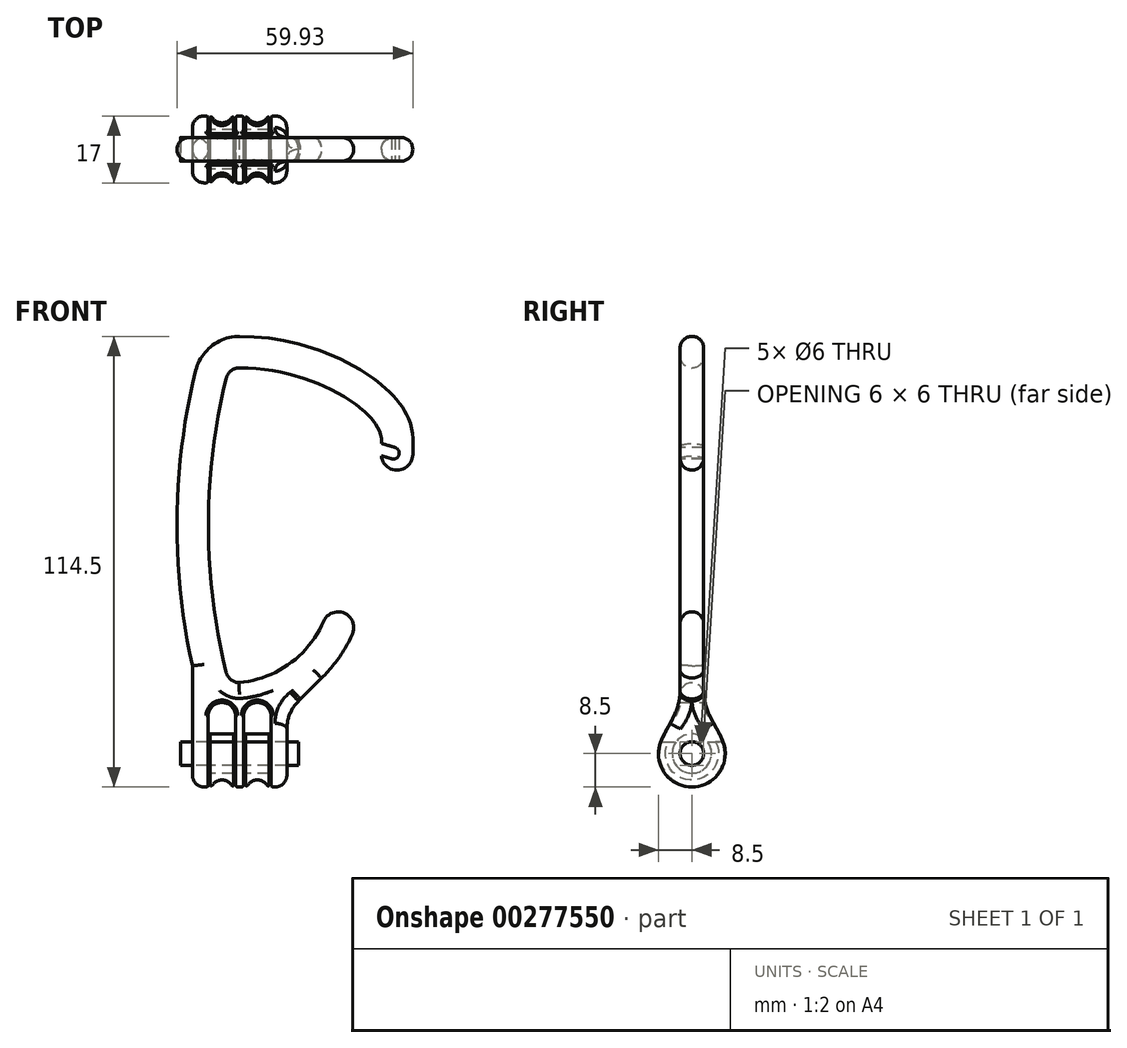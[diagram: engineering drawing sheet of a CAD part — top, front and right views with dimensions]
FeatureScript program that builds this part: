
annotation { "Feature Type Name" : "Feature", "Feature Type Description" : "" }
export const myFeature = defineFeature(function(context is Context, id is Id, definition is map)
    precondition{}
    {
        {
            var Q0;
            Q0=qCreatedBy(makeId("Front.planeOp"),FACE);
            var sketch = newSketch(context, id + "F0", { "sketchPlane" : qUnion([Q0])});
            skPoint(sketch, "E0.middle", {"position": v(0, 0) * mm});
            skLineSegment(sketch, "E1", {"start": v(0, 91.6) * mm, "end": v(0, -27.1) * mm, "construction": true});
            skLineSegment(sketch, "E2", {"start": v(-37.43, 0) * mm, "end": v(37.27, 0) * mm, "construction": true});
            skLineSegment(sketch, "E3", {"start": v(-37.5, -22) * mm, "end": v(37.5, -22) * mm, "construction": true});
            skLineSegment(sketch, "E4", {"start": v(-4.5, -27) * mm, "end": v(-4.5, -17) * mm, "construction": true});
            skLineSegment(sketch, "E5", {"start": v(4.5, -27) * mm, "end": v(4.5, -17) * mm, "construction": true});
            skLineSegment(sketch, "E6", {"start": v(-5, 80) * mm, "end": v(5, 80) * mm, "construction": true});
            skSolve(sketch);
        }
        {
            var Q0;
            Q0=qCreatedBy(makeId("Front.planeOp"),FACE);
            var sketch = newSketch(context, id + "F1", { "sketchPlane" : qUnion([Q0])});
            skLineSegment(sketch, "E7", {"start": v(-7.5, -17) * mm, "end": v(-7.5, -14) * mm});
            skLineSegment(sketch, "E8", {"start": v(-1.5, -14) * mm, "end": v(-1.5, -17) * mm});
            skArc(sketch, "E9", {"start": v(-7.04, -13.87) * mm, "mid": v(-4.5, -15.27) * mm, "end": v(-1.96, -13.87) * mm});
            skPoint(sketch, "E10.visualSharp", {"position": v(-7.5, -12.27) * mm});
            skArc(sketch, "E10.filletArc", {"start": v(-7.04, -13.87) * mm, "mid": v(-7.32, -13.76) * mm, "end": v(-7.5, -14) * mm});
            skPoint(sketch, "E11.visualSharp", {"position": v(-1.5, -12.27) * mm});
            skArc(sketch, "E11.filletArc", {"start": v(-1.5, -14) * mm, "mid": v(-1.68, -13.76) * mm, "end": v(-1.96, -13.87) * mm});
            skLineSegment(sketch, "E12", {"start": v(-7.5, -17) * mm, "end": v(-1.5, -17) * mm});
            skArc(sketch, "E13.MirrorCS", {"start": v(7.04, -13.87) * mm, "mid": v(7.32, -13.76) * mm, "end": v(7.5, -14) * mm});
            skArc(sketch, "E14.MirrorCS", {"start": v(1.5, -14) * mm, "mid": v(1.68, -13.76) * mm, "end": v(1.96, -13.87) * mm});
            skArc(sketch, "E15.MirrorCS", {"start": v(7.04, -13.87) * mm, "mid": v(4.5, -15.27) * mm, "end": v(1.96, -13.87) * mm});
            skPoint(sketch, "E16.MirrorP", {"position": v(7.5, -12.27) * mm});
            skPoint(sketch, "E17.MirrorP", {"position": v(1.5, -12.27) * mm});
            skLineSegment(sketch, "E18.MirrorCS", {"start": v(1.5, -14) * mm, "end": v(1.5, -17) * mm});
            skLineSegment(sketch, "E19.MirrorCS", {"start": v(7.5, -17) * mm, "end": v(1.5, -17) * mm});
            skLineSegment(sketch, "E20.MirrorCS", {"start": v(7.5, -17) * mm, "end": v(7.5, -14) * mm});
            skSolve(sketch);
        }
        {
            var Q0;
            Q0 = qSketchRegion(id + "F1", true);
            var Q1;
            Q1=sQuery(id+"F0.wireOp",EDGE,"E3");
            revolve(context, id + "F2", {"entities" : qUnion([Q0]), "axis" : qUnion([Q1]), "revolveType" : RevolveType.FULL});
        }
        {
            var Q0;
            Q0=qCreatedBy(makeId("Front.planeOp"),FACE);
            var sketch = newSketch(context, id + "F3", { "sketchPlane" : qUnion([Q0])});
            skPoint(sketch, "E21", {"position": v(0, 80) * mm});
            skPoint(sketch, "E22", {"position": v(40, 58) * mm});
            skArc(sketch, "E23", {"start": v(0, 80) * mm, "mid": v(-4.63, 78.4) * mm, "end": v(-7.28, 74.3) * mm});
            skPoint(sketch, "E24", {"position": v(25, 10) * mm});
            skLineSegment(sketch, "E25", {"start": v(40, 58) * mm, "end": v(40, 54) * mm});
            skArc(sketch, "E26", {"start": v(-7.28, -2.3) * mm, "mid": v(-4.63, -6.4) * mm, "end": v(0, -8) * mm});
            skArc(sketch, "E27", {"start": v(0, -8) * mm, "mid": v(14.99, -2.45) * mm, "end": v(25, 10) * mm});
            skFitSpline(sketch, "E28", {"points": [v(0, 80) * mm, v(40, 58) * mm], "startDerivative": vector(60, 0) * mm, "endDerivative": vector(0, -30) * mm});
            skPoint(sketch, "E29", {"position": v(40, 54) * mm});
            skArc(sketch, "E30", {"start": v(-7.28, 74.3) * mm, "mid": v(-11.93, 36) * mm, "end": v(-7.28, -2.3) * mm});
            skSolve(sketch);
        }
        {
            var Q0;
            Q0=qCreatedBy(makeId("Top.planeOp"),FACE);
            cPlane(context, id + "F4", {"entities" : qUnion([Q0]), "cplaneType" : CPlaneType.OFFSET, "offset" : 54 * mm, "width" : 150 * mm, "height" : 150 * mm});
        }
        {
            var Q0;
            Q0=qCreatedBy(id+"F4.planeOp",FACE);
            var sketch = newSketch(context, id + "F5", { "sketchPlane" : qUnion([Q0])});
            skLineSegment(sketch, "E31.bottom", {"start": v(39, -3) * mm, "end": v(41, -3) * mm});
            skLineSegment(sketch, "E31.top", {"start": v(39, 3) * mm, "end": v(41, 3) * mm});
            skArc(sketch, "E32", {"start": v(39, 3) * mm, "mid": v(36, 0) * mm, "end": v(39, -3) * mm});
            skArc(sketch, "E33", {"start": v(41, -3) * mm, "mid": v(44, 0) * mm, "end": v(41, 3) * mm});
            skSolve(sketch);
        }
        {
            var Q0;
            Q0=makeQuery(id+"F5.imprint","IMPRINT",FACE,{"disambiguationData":[TD([[makeQuery(id+"F5.imprint","IMPRINT",EDGE,{"derivedFrom":sQuery(id+"F5.wireOp",EDGE,"E31.bottom")}),1.0]])]});
            var Q1;
            Q1=sQuery(id+"F3.wireOp",EDGE,"E25");
            var Q2;
            Q2=sQuery(id+"F3.wireOp",EDGE,"E28");
            var Q3;
            Q3=sQuery(id+"F3.wireOp",EDGE,"E23");
            var Q4;
            Q4=sQuery(id+"F3.wireOp",EDGE,"57eace3e-279f-4ff9-bc42-776380e31d05");
            var Q5;
            Q5=sQuery(id+"F3.wireOp",EDGE,"E26");
            var Q6;
            Q6=sQuery(id+"F3.wireOp",EDGE,"E27");
            var Q7;
            Q7=sQuery(id+"F3.wireOp",EDGE,"E30");
            sweep(context, id + "F6", {"profiles" : qUnion([Q0]), "path" : qUnion([Q1, Q2, Q3, Q4, Q5, Q6, Q7])});
        }
        {
            var Q0;
            Q0=qCreatedBy(makeId("Front.planeOp"),FACE);
            var sketch = newSketch(context, id + "F7", { "sketchPlane" : qUnion([Q0])});
            skLineSegment(sketch, "E34", {"start": v(-8, -17.5) * mm, "end": v(-8, -30.5) * mm});
            skLineSegment(sketch, "E35", {"start": v(-8, -30.5) * mm, "end": v(-12, -30.5) * mm});
            skLineSegment(sketch, "E36", {"start": v(-12, -30.5) * mm, "end": v(-12, -14.5) * mm});
            skLineSegment(sketch, "E37", {"start": v(0, -30.5) * mm, "end": v(-1, -30.5) * mm});
            skLineSegment(sketch, "E38", {"start": v(-1, -30.5) * mm, "end": v(-1, -17.5) * mm});
            skArc(sketch, "E39", {"start": v(-1, -17.5) * mm, "mid": v(-4.5, -14) * mm, "end": v(-8, -17.5) * mm});
            skLineSegment(sketch, "E40.MirrorCS", {"start": v(0, -30.5) * mm, "end": v(1, -30.5) * mm});
            skArc(sketch, "E41.MirrorCS", {"start": v(1, -17.5) * mm, "mid": v(4.5, -14) * mm, "end": v(8, -17.5) * mm});
            skLineSegment(sketch, "E42.MirrorCS", {"start": v(8, -17.5) * mm, "end": v(8, -30.5) * mm});
            skLineSegment(sketch, "E43.MirrorCS", {"start": v(1, -30.5) * mm, "end": v(1, -17.5) * mm});
            skLineSegment(sketch, "E44.MirrorCS", {"start": v(12, -30.5) * mm, "end": v(12, -15.77) * mm});
            skLineSegment(sketch, "E45.MirrorCS", {"start": v(8, -30.5) * mm, "end": v(12, -30.5) * mm});
            skArc(sketch, "E46", {"start": v(-7.17, -2.73) * mm, "mid": v(-4.46, -6.56) * mm, "end": v(0, -8.03) * mm});
            skArc(sketch, "E47", {"start": v(0, -8.03) * mm, "mid": v(9.66, -5.53) * mm, "end": v(17.97, 0) * mm});
            skLineSegment(sketch, "E48", {"start": v(17.97, 0) * mm, "end": v(20.8, -2.83) * mm});
            skLineSegment(sketch, "E49", {"start": v(-12, -14.5) * mm, "end": v(-12, 25.5) * mm});
            skLineSegment(sketch, "E50", {"start": v(-12, 25.5) * mm, "end": v(-7.17, -2.73) * mm});
            skLineSegment(sketch, "E51", {"start": v(20.8, -2.83) * mm, "end": v(14.93, -8.7) * mm});
            skPoint(sketch, "E52.visualSharp", {"position": v(12, -11.63) * mm});
            skArc(sketch, "E52.filletArc", {"start": v(14.93, -8.7) * mm, "mid": v(12.76, -11.94) * mm, "end": v(12, -15.77) * mm});
            skSolve(sketch);
        }
        {
            var Q0;
            Q0=makeQuery(id+"F7.imprint","IMPRINT",FACE,{"disambiguationData":[TD([[makeQuery(id+"F7.imprint","IMPRINT",EDGE,{"derivedFrom":sQuery(id+"F7.wireOp",EDGE,"E34")}),-1.0]])]});
            extrude(context, id + "F8", {"entities" : qUnion([Q0]), "operationType" : NewBodyOperationType.ADD, "endBound" : BoundingType.SYMMETRIC, "depth" : 18 * mm});
        }
        {
            var Q0;
            Q0=qCreatedBy(makeId("Right.planeOp"),FACE);
            var sketch = newSketch(context, id + "F9", { "sketchPlane" : qUnion([Q0])});
            skArc(sketch, "E53", {"start": v(-8.5, -22) * mm, "mid": v(0, -30.5) * mm, "end": v(8.5, -22) * mm});
            skFitSpline(sketch, "E54", {"points": [v(8.5, -22) * mm, v(3, -6) * mm], "startDerivative": vector(0, 15) * mm, "endDerivative": vector(0, 21) * mm});
            skFitSpline(sketch, "E55.MirrorCS", {"points": [v(-8.5, -22) * mm, v(-3, -6) * mm], "startDerivative": vector(0, 15) * mm, "endDerivative": vector(0, 21) * mm});
            skLineSegment(sketch, "E56", {"start": v(-3, -6) * mm, "end": v(-3, 30) * mm});
            skLineSegment(sketch, "E57", {"start": v(-3, 30) * mm, "end": v(-13, 30) * mm});
            skLineSegment(sketch, "E58", {"start": v(-13, -40) * mm, "end": v(-13, 30) * mm});
            skLineSegment(sketch, "E59.MirrorCS", {"start": v(13, -40) * mm, "end": v(13, 30) * mm});
            skLineSegment(sketch, "E60.MirrorCS", {"start": v(3, 30) * mm, "end": v(13, 30) * mm});
            skLineSegment(sketch, "E61", {"start": v(3, 30) * mm, "end": v(3, -6) * mm});
            skCircle(sketch, "E62", {"center": v(0, -22) * mm, "radius": 3 * mm});
            skLineSegment(sketch, "E63", {"start": v(13, -40) * mm, "end": v(-13, -40) * mm});
            skSolve(sketch);
        }
        {
            var Q0;
            Q0=makeQuery(id+"F9.imprint","IMPRINT",FACE,{"disambiguationData":[TD([[makeQuery(id+"F9.imprint","IMPRINT",EDGE,{"derivedFrom":sQuery(id+"F9.wireOp",EDGE,"E53")}),-1.0]])]});
            extrude(context, id + "F10", {"entities" : qUnion([Q0]), "operationType" : NewBodyOperationType.REMOVE, "endBound" : BoundingType.SYMMETRIC, "depth" : 100 * mm});
        }
        {
            var Q0;
            Q0=makeQuery(id+"F6.opSweep","CAP_FACE",FACE,{"disambiguationData":[OSD([sQuery(id+"F3.wireOp",VERTEX,"E27.end"),sQuery(id+"F5.wireOp",EDGE,"E31.bottom"),sQuery(id+"F5.wireOp",EDGE,"E31.top"),sQuery(id+"F5.wireOp",EDGE,"E32"),sQuery(id+"F5.wireOp",EDGE,"E33")])],"isStart":false});
            var sketch = newSketch(context, id + "F11", { "sketchPlane" : qUnion([Q0])});
            skLineSegment(sketch, "E64", {"start": v(18.99, -3) * mm, "end": v(18.99, 3) * mm});
            skLineSegment(sketch, "E65", {"start": v(18.99, 3) * mm, "end": v(19.99, 3) * mm});
            skLineSegment(sketch, "E66", {"start": v(18.99, -3) * mm, "end": v(19.99, -3) * mm});
            skArc(sketch, "E67", {"start": v(19.99, -3) * mm, "mid": v(22.99, 0) * mm, "end": v(19.99, 3) * mm});
            skLineSegment(sketch, "E68", {"start": v(18.99, 4.4) * mm, "end": v(18.99, -4.85) * mm, "construction": true});
            skSolve(sketch);
        }
        {
            var Q0;
            Q0 = qSketchRegion(id + "F11", true);
            var Q1;
            Q1=sQuery(id+"F11.wireOp",EDGE,"E68");
            revolve(context, id + "F12", {"operationType" : NewBodyOperationType.ADD, "entities" : qUnion([Q0]), "axis" : qUnion([Q1]), "revolveType" : RevolveType.FULL});
        }
        {
            var Q0;
            Q0=makeQuery(id+"F6.opSweep","CAP_FACE",FACE,{"disambiguationData":[OSD([sQuery(id+"F3.wireOp",VERTEX,"E25.end"),sQuery(id+"F5.wireOp",EDGE,"E31.bottom"),sQuery(id+"F5.wireOp",EDGE,"E31.top"),sQuery(id+"F5.wireOp",EDGE,"E32"),sQuery(id+"F5.wireOp",EDGE,"E33")])],"isStart":true});
            var sketch = newSketch(context, id + "F13", { "sketchPlane" : qUnion([Q0])});
            skLineSegment(sketch, "E69", {"start": v(40, -3) * mm, "end": v(40, 3) * mm});
            skLineSegment(sketch, "E70", {"start": v(40, -3) * mm, "end": v(41, -3) * mm});
            skLineSegment(sketch, "E71", {"start": v(40, 4.32) * mm, "end": v(40, -4) * mm, "construction": true});
            skLineSegment(sketch, "E72", {"start": v(40, 3) * mm, "end": v(41, 3) * mm});
            skArc(sketch, "E73", {"start": v(41, -3) * mm, "mid": v(44, 0) * mm, "end": v(41, 3) * mm});
            skSolve(sketch);
        }
        {
            var Q0;
            Q0 = qSketchRegion(id + "F13", true);
            var Q1;
            Q1=sQuery(id+"F13.wireOp",EDGE,"E71");
            revolve(context, id + "F14", {"operationType" : NewBodyOperationType.ADD, "entities" : qUnion([Q0]), "axis" : qUnion([Q1]), "revolveType" : RevolveType.FULL});
        }
        {
            var Q0;
            Q0=qCreatedBy(makeId("Front.planeOp"),FACE);
            var sketch = newSketch(context, id + "F15", { "sketchPlane" : qUnion([Q0])});
            skPoint(sketch, "E74", {"position": v(23.17, 6.44) * mm});
            skPoint(sketch, "E75", {"position": v(20.89, 3.16) * mm});
            skCircle(sketch, "E76", {"center": v(23.17, 6.44) * mm, "radius": 50.45 * mm, "construction": true});
            skArc(sketch, "E77", {"start": v(37.63, 54.8) * mm, "mid": v(37.63, 54.79) * mm, "end": v(37.62, 54.78) * mm});
            skLineSegment(sketch, "E78", {"start": v(39.05, 54.32) * mm, "end": v(39.53, 55.75) * mm});
            skLineSegment(sketch, "E79", {"start": v(39.05, 54.32) * mm, "end": v(38.58, 52.9) * mm});
            skLineSegment(sketch, "E80", {"start": v(39.05, 54.32) * mm, "end": v(33.18, 56.27) * mm, "construction": true});
            skArc(sketch, "E81.trimOffspring", {"start": v(38.58, 52.9) * mm, "mid": v(40.48, 53.85) * mm, "end": v(39.53, 55.75) * mm});
            skArc(sketch, "E82", {"start": v(39.53, 55.75) * mm, "mid": v(37.61, 56.32) * mm, "end": v(35.68, 56.86) * mm});
            skArc(sketch, "E83", {"start": v(38.58, 52.9) * mm, "mid": v(36.66, 53.47) * mm, "end": v(34.74, 54) * mm});
            skLineSegment(sketch, "E84", {"start": v(35.68, 56.86) * mm, "end": v(34.74, 54) * mm});
            skSolve(sketch);
        }
        {
            var Q0;
            Q0 = qSketchRegion(id + "F15", true);
            extrude(context, id + "F16", {"entities" : qUnion([Q0]), "operationType" : NewBodyOperationType.REMOVE, "endBound" : BoundingType.SYMMETRIC, "oppositeDirection" : true, "depth" : 25 * mm});
        }
        {
            var Q0;
            Q0=makeQuery(id+"F10.boolean.opBoolean","INTERSECT",EDGE,{"derivedFrom":[makeQuery(id+"F8.opExtrude","SWEPT_FACE",FACE,{"disambiguationData":[OSD([sQuery(id+"F7.wireOp",EDGE,"E36"),sQuery(id+"F7.wireOp",EDGE,"E49")])]}),makeQuery(id+"F10.opExtrude","SWEPT_FACE",FACE,{"disambiguationData":[OSD([sQuery(id+"F9.wireOp",EDGE,"E56")])]})]});
            var Q1;
            Q1=makeQuery(id+"F10.boolean.opBoolean","INTERSECT",EDGE,{"derivedFrom":[makeQuery(id+"F8.opExtrude","SWEPT_FACE",FACE,{"disambiguationData":[OSD([sQuery(id+"F7.wireOp",EDGE,"E36"),sQuery(id+"F7.wireOp",EDGE,"E49")])]}),makeQuery(id+"F10.opExtrude","SWEPT_FACE",FACE,{"disambiguationData":[OSD([sQuery(id+"F9.wireOp",EDGE,"E61")])]})]});
            var Q2;
            Q2=makeQuery(id+"F10.boolean.opBoolean","INTERSECT",EDGE,{"derivedFrom":[makeQuery(id+"F8.opExtrude","SWEPT_FACE",FACE,{"disambiguationData":[OSD([sQuery(id+"F7.wireOp",EDGE,"E36"),sQuery(id+"F7.wireOp",EDGE,"E49")])]}),makeQuery(id+"F10.opExtrude","SWEPT_FACE",FACE,{"disambiguationData":[OSD([sQuery(id+"F9.wireOp",EDGE,"E55.MirrorCS")])]})]});
            var Q3;
            Q3=makeQuery(id+"F10.boolean.opBoolean","INTERSECT",EDGE,{"derivedFrom":[makeQuery(id+"F8.opExtrude","SWEPT_FACE",FACE,{"disambiguationData":[OSD([sQuery(id+"F7.wireOp",EDGE,"E36"),sQuery(id+"F7.wireOp",EDGE,"E49")])]}),makeQuery(id+"F10.opExtrude","SWEPT_FACE",FACE,{"disambiguationData":[OSD([sQuery(id+"F9.wireOp",EDGE,"E53")])]})]});
            var Q4;
            Q4=makeQuery(id+"F10.boolean.opBoolean","INTERSECT",EDGE,{"derivedFrom":[makeQuery(id+"F8.opExtrude","SWEPT_FACE",FACE,{"disambiguationData":[OSD([sQuery(id+"F7.wireOp",EDGE,"E36"),sQuery(id+"F7.wireOp",EDGE,"E49")])]}),makeQuery(id+"F10.opExtrude","SWEPT_FACE",FACE,{"disambiguationData":[OSD([sQuery(id+"F9.wireOp",EDGE,"E54")])]})]});
            fillet(context, id + "F17", {"entities" : qUnion([Q0, Q1, Q2, Q3, Q4]), "radius" : 3 * mm, "tangentPropagation" : true, "allowEdgeOverflow" : false});
        }
        {
            var Q0;
            Q0=qCreatedBy(makeId("Front.planeOp"),FACE);
            var sketch = newSketch(context, id + "F18", { "sketchPlane" : qUnion([Q0])});
            skArc(sketch, "E85", {"start": v(8, -12.5) * mm, "mid": v(4.5, -9) * mm, "end": v(1, -12.5) * mm});
            skLineSegment(sketch, "E86.top", {"start": v(8, -19) * mm, "end": v(1, -19) * mm});
            skLineSegment(sketch, "E86.left", {"start": v(8, -12.5) * mm, "end": v(8, -19) * mm});
            skLineSegment(sketch, "E86.right", {"start": v(1, -12.5) * mm, "end": v(1, -19) * mm});
            skLineSegment(sketch, "E87.MirrorCS", {"start": v(-8, -12.5) * mm, "end": v(-8, -19) * mm});
            skLineSegment(sketch, "E88.MirrorCS", {"start": v(-1, -12.5) * mm, "end": v(-1, -19) * mm});
            skLineSegment(sketch, "E89.MirrorCS", {"start": v(-8, -19) * mm, "end": v(-1, -19) * mm});
            skArc(sketch, "E90.MirrorCS", {"start": v(-8, -12.5) * mm, "mid": v(-4.5, -9) * mm, "end": v(-1, -12.5) * mm});
            skSolve(sketch);
        }
        {
            var Q0;
            Q0 = qSketchRegion(id + "F18", true);
            extrude(context, id + "F19", {"entities" : qUnion([Q0]), "operationType" : NewBodyOperationType.REMOVE, "endBound" : BoundingType.SYMMETRIC, "depth" : 25 * mm});
        }
        {
            var Q0;
            Q0=makeQuery(id+"F10.boolean.opBoolean","INTERSECT",EDGE,{"derivedFrom":[makeQuery(id+"F8.opExtrude","SWEPT_FACE",FACE,{"disambiguationData":[OSD([sQuery(id+"F7.wireOp",EDGE,"E51")])]}),makeQuery(id+"F10.opExtrude","SWEPT_FACE",FACE,{"disambiguationData":[OSD([sQuery(id+"F9.wireOp",EDGE,"E56")])]})]});
            fillet(context, id + "F20", {"entities" : qUnion([Q0]), "radius" : 3 * mm, "tangentPropagation" : true, "allowEdgeOverflow" : false});
        }
        {
            var Q0;
            Q0=qCreatedBy(makeId("Front.planeOp"),FACE);
            var sketch = newSketch(context, id + "F21", { "sketchPlane" : qUnion([Q0])});
            skLineSegment(sketch, "E91.bottom", {"start": v(7.5, -17) * mm, "end": v(1.5, -17) * mm});
            skLineSegment(sketch, "E91.top", {"start": v(7.5, -19) * mm, "end": v(1.5, -19) * mm});
            skLineSegment(sketch, "E91.left", {"start": v(7.5, -17) * mm, "end": v(7.5, -19) * mm});
            skLineSegment(sketch, "E91.right", {"start": v(1.5, -17) * mm, "end": v(1.5, -19) * mm});
            skLineSegment(sketch, "E92.MirrorCS", {"start": v(-7.5, -17) * mm, "end": v(-1.5, -17) * mm});
            skLineSegment(sketch, "E93.MirrorCS", {"start": v(-7.5, -17) * mm, "end": v(-7.5, -19) * mm});
            skLineSegment(sketch, "E94.MirrorCS", {"start": v(-1.5, -17) * mm, "end": v(-1.5, -19) * mm});
            skLineSegment(sketch, "E95.MirrorCS", {"start": v(-7.5, -19) * mm, "end": v(-1.5, -19) * mm});
            skSolve(sketch);
        }
        {
            var Q0;
            Q0 = qSketchRegion(id + "F21", true);
            var Q1;
            Q1=sQuery(id+"F0.wireOp",EDGE,"E3");
            revolve(context, id + "F22", {"entities" : qUnion([Q0]), "axis" : qUnion([Q1]), "revolveType" : RevolveType.FULL});
        }
        {
            var Q0;
            Q0=qCreatedBy(makeId("Right.planeOp"),FACE);
            var sketch = newSketch(context, id + "F23", { "sketchPlane" : qUnion([Q0])});
            skCircle(sketch, "E96", {"center": v(0, -22) * mm, "radius": 3 * mm});
            skSolve(sketch);
        }
        {
            var Q0;
            Q0 = qSketchRegion(id + "F23", true);
            extrude(context, id + "F24", {"entities" : qUnion([Q0]), "operationType" : NewBodyOperationType.REMOVE, "endBound" : BoundingType.SYMMETRIC, "depth" : 30 * mm});
        }
        {
            var Q0;
            Q0=makeQuery(id+"F19.boolean.opBoolean","INTERSECT",EDGE,{"derivedFrom":[makeQuery(id+"F10.boolean.opBoolean","COPY",FACE,{"derivedFrom":makeQuery(id+"F10.opExtrude","SWEPT_FACE",FACE,{"disambiguationData":[OSD([sQuery(id+"F9.wireOp",EDGE,"E55.MirrorCS")])]})}),makeQuery(id+"F19.opExtrude","SWEPT_FACE",FACE,{"disambiguationData":[OSD([sQuery(id+"F18.wireOp",EDGE,"E87.MirrorCS")])]})]});
            var Q1;
            Q1=makeQuery(id+"F19.boolean.opBoolean","INTERSECT",EDGE,{"derivedFrom":[makeQuery(id+"F10.boolean.opBoolean","COPY",FACE,{"derivedFrom":makeQuery(id+"F10.opExtrude","SWEPT_FACE",FACE,{"disambiguationData":[OSD([sQuery(id+"F9.wireOp",EDGE,"E55.MirrorCS")])]})}),makeQuery(id+"F19.opExtrude","SWEPT_FACE",FACE,{"disambiguationData":[OSD([sQuery(id+"F18.wireOp",EDGE,"E86.right")])]})]});
            fillet(context, id + "F25", {"entities" : qUnion([Q0, Q1]), "radius" : .5 * mm, "tangentPropagation" : true, "allowEdgeOverflow" : false});
        }
        {
            var Q0;
            Q0=qCreatedBy(makeId("Right.planeOp"),FACE);
            var sketch = newSketch(context, id + "F26", { "sketchPlane" : qUnion([Q0])});
            skCircle(sketch, "E97", {"center": v(0, -22) * mm, "radius": 3 * mm});
            skSolve(sketch);
        }
        {
            var Q0;
            Q0 = qSketchRegion(id + "F26", true);
            extrude(context, id + "F27", {"entities" : qUnion([Q0]), "endBound" : BoundingType.SYMMETRIC, "depth" : 30 * mm});
        }
    });
